# Revit family: LeL Oliver 3.3
name_source: partatom
category: Lighting Fixtures
units: mm (PartAtom-declared; Revit-internal decimal feet)

## family parameters
Always vertical = No
Cut with Voids When Loaded = No
Light Source = No
OmniClass Number = 23.80.70.00
OmniClass Title = Lighting
Part Type = Normal
Room Calculation Point = No
Round Connector Dimension = Use Diameter
Shared = No
Work Plane-Based = Yes

## types (5) — shared parameters
Apparent Load = 93 VA
CCT = 3000 K
Default Elevation = 1219 mm
Description = Outdoor Projectors
IK = IK09
IP = IP66
Lamp = LED
Manufacturer = L&L Luce&Light srl
Model = LV33
Rated Power supply = 230 V
URL = https://www.lucelight.it
Wattage_2 = 93 W
Weight = 8.80 kg

## per-type parameters (varying)
| type | Photometry |
| S 10° 93W | LV33 Light source : S 10° 93W |
| M 24° 93W | LV33 Light source : M 24° 93W |
| L 34° 93W | LV33 Light source : L 34° 93W |
| K 55° 93W | LV33 Light source : K 55° 93W |
| X 11°x66° 93W | LV33 Light source : X 11°x66° 93W |
